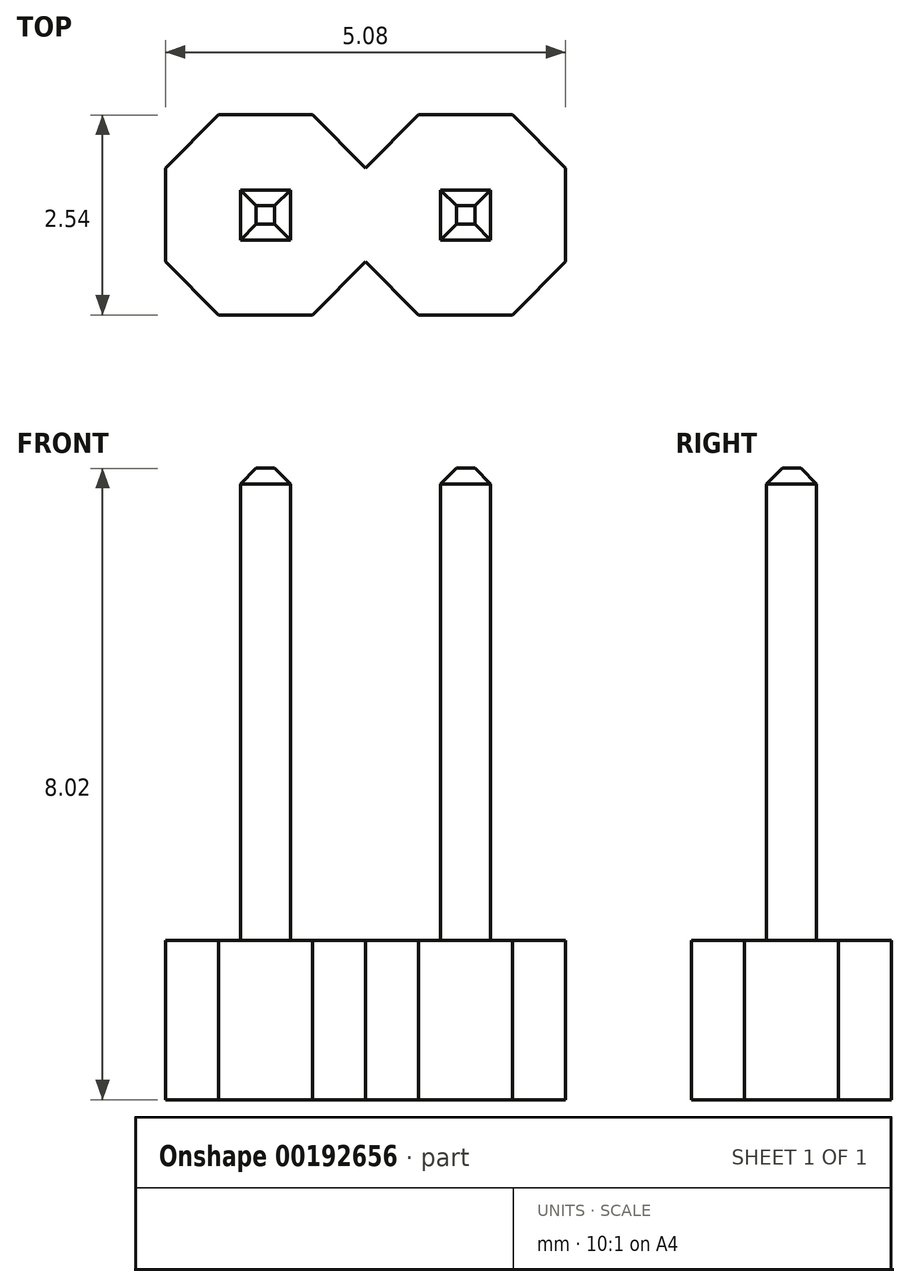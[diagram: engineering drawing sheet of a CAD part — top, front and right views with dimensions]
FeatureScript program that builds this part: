
annotation { "Feature Type Name" : "Feature", "Feature Type Description" : "" }
export const myFeature = defineFeature(function(context is Context, id is Id, definition is map)
    precondition{}
    {
        {
            var Q0;
            Q0=qCreatedBy(makeId("Top.planeOp"),FACE);
            var sketch = newSketch(context, id + "F0", { "sketchPlane" : qUnion([Q0])});
            skLineSegment(sketch, "E0.0", {"start": v(-1.87, 1.27) * mm, "end": v(-0.68, 1.27) * mm});
            skLineSegment(sketch, "E0.1", {"start": v(-0.68, 1.27) * mm, "end": v(0, 0.6) * mm});
            skLineSegment(sketch, "E0.2", {"start": v(0, 0.6) * mm, "end": v(0, -0.6) * mm});
            skLineSegment(sketch, "E0.3", {"start": v(0, -0.6) * mm, "end": v(-0.67, -1.27) * mm});
            skLineSegment(sketch, "E0.4", {"start": v(-0.67, -1.27) * mm, "end": v(-1.86, -1.27) * mm});
            skLineSegment(sketch, "E0.5", {"start": v(-1.86, -1.27) * mm, "end": v(-2.54, -0.6) * mm});
            skLineSegment(sketch, "E0.6", {"start": v(-2.54, -0.6) * mm, "end": v(-2.54, 0.6) * mm});
            skLineSegment(sketch, "E0.7", {"start": v(-2.54, 0.6) * mm, "end": v(-1.87, 1.27) * mm});
            skPoint(sketch, "E0.0.midPoint", {"position": v(-1.27, 1.27) * mm});
            skLineSegment(sketch, "E1.MirrorCS", {"start": v(1.87, 1.27) * mm, "end": v(0.68, 1.27) * mm});
            skLineSegment(sketch, "E2.MirrorCS", {"start": v(0.68, 1.27) * mm, "end": v(0, 0.6) * mm});
            skLineSegment(sketch, "E3.MirrorCS", {"start": v(0, -0.6) * mm, "end": v(0.67, -1.27) * mm});
            skPoint(sketch, "E4.MirrorP", {"position": v(1.27, 1.27) * mm});
            skLineSegment(sketch, "E5.MirrorCS", {"start": v(0.67, -1.27) * mm, "end": v(1.86, -1.27) * mm});
            skLineSegment(sketch, "E6.MirrorCS", {"start": v(1.87, -1.27) * mm, "end": v(2.54, -0.6) * mm});
            skLineSegment(sketch, "E7.MirrorCS", {"start": v(2.54, -0.6) * mm, "end": v(2.54, 0.6) * mm});
            skLineSegment(sketch, "E8.MirrorCS", {"start": v(2.54, 0.6) * mm, "end": v(1.87, 1.27) * mm});
            skSolve(sketch);
        }
        {
            var Q0;
            Q0 = qSketchRegion(id + "F0", true);
            extrude(context, id + "F1", {"entities" : qUnion([Q0]), "depth" : 2.02 * mm});
        }
        {
            var Q0;
            Q0=makeQuery(id+"F1.opExtrude","CAP_FACE",FACE,{"disambiguationData":[OSD([sQuery(id+"F0.wireOp",EDGE,"E0.0"),sQuery(id+"F0.wireOp",EDGE,"E0.1"),sQuery(id+"F0.wireOp",EDGE,"E0.3"),sQuery(id+"F0.wireOp",EDGE,"E0.4"),sQuery(id+"F0.wireOp",EDGE,"E0.5"),sQuery(id+"F0.wireOp",EDGE,"E0.6"),sQuery(id+"F0.wireOp",EDGE,"E0.7"),sQuery(id+"F0.wireOp",EDGE,"E1.MirrorCS"),sQuery(id+"F0.wireOp",EDGE,"E2.MirrorCS"),sQuery(id+"F0.wireOp",EDGE,"E3.MirrorCS"),sQuery(id+"F0.wireOp",EDGE,"E5.MirrorCS"),sQuery(id+"F0.wireOp",EDGE,"E6.MirrorCS"),sQuery(id+"F0.wireOp",EDGE,"E7.MirrorCS"),sQuery(id+"F0.wireOp",EDGE,"E8.MirrorCS")])],"isStart":false});
            var sketch = newSketch(context, id + "F2", { "sketchPlane" : qUnion([Q0])});
            skLineSegment(sketch, "E9.bottom", {"start": v(-1.59, 0.32) * mm, "end": v(-0.95, 0.32) * mm});
            skLineSegment(sketch, "E9.top", {"start": v(-1.59, -0.32) * mm, "end": v(-0.95, -0.32) * mm});
            skLineSegment(sketch, "E9.left", {"start": v(-1.59, 0.32) * mm, "end": v(-1.59, -0.32) * mm});
            skLineSegment(sketch, "E9.right", {"start": v(-0.95, 0.32) * mm, "end": v(-0.95, -0.32) * mm});
            skPoint(sketch, "E9.middle", {"position": v(-1.27, 0) * mm});
            skLineSegment(sketch, "E10.bottom", {"start": v(0.95, 0.32) * mm, "end": v(1.59, 0.32) * mm});
            skLineSegment(sketch, "E10.top", {"start": v(0.95, -0.32) * mm, "end": v(1.59, -0.32) * mm});
            skLineSegment(sketch, "E10.left", {"start": v(0.95, 0.32) * mm, "end": v(0.95, -0.32) * mm});
            skLineSegment(sketch, "E10.right", {"start": v(1.59, 0.32) * mm, "end": v(1.59, -0.32) * mm});
            skPoint(sketch, "E10.middle", {"position": v(1.27, 0) * mm});
            skSolve(sketch);
        }
        {
            var Q0;
            Q0 = qSketchRegion(id + "F2", true);
            extrude(context, id + "F3", {"entities" : qUnion([Q0]), "depth" : 6 * mm});
        }
        {
            var Q0;
            Q0=makeQuery(id+"F3.opExtrude","CAP_FACE",FACE,{"disambiguationData":[OSD([sQuery(id+"F2.wireOp",EDGE,"E9.bottom"),sQuery(id+"F2.wireOp",EDGE,"E9.top"),sQuery(id+"F2.wireOp",EDGE,"E9.left"),sQuery(id+"F2.wireOp",EDGE,"E9.right")])],"isStart":false});
            var Q1;
            Q1=makeQuery(id+"F3.opExtrude","CAP_FACE",FACE,{"disambiguationData":[OSD([sQuery(id+"F2.wireOp",EDGE,"E10.bottom"),sQuery(id+"F2.wireOp",EDGE,"E10.top"),sQuery(id+"F2.wireOp",EDGE,"E10.left"),sQuery(id+"F2.wireOp",EDGE,"E10.right")])],"isStart":false});
            chamfer(context, id + "F4", {"entities" : qUnion([Q0, Q1]), "width" : .2 * mm, "tangentPropagation" : true});
        }
    });
